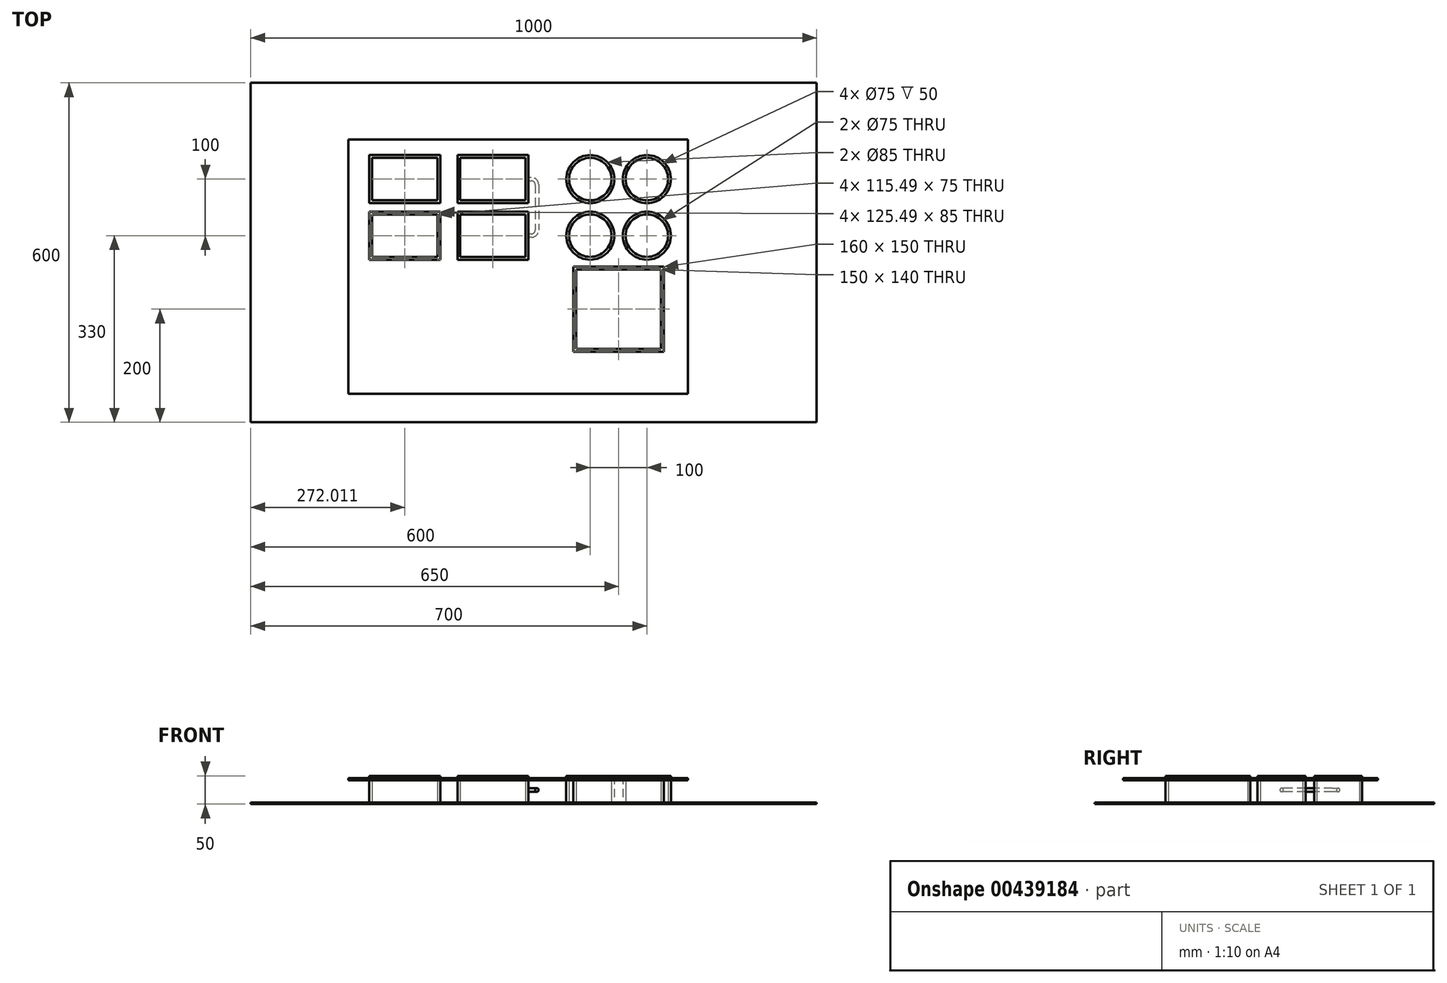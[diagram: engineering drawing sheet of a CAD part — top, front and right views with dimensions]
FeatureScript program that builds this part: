
annotation { "Feature Type Name" : "Feature", "Feature Type Description" : "" }
export const myFeature = defineFeature(function(context is Context, id is Id, definition is map)
    precondition{}
    {
        {
            var Q0;
            Q0=qCreatedBy(makeId("Top.planeOp"),FACE);
            var sketch = newSketch(context, id + "F0", { "sketchPlane" : qUnion([Q0])});
            skLineSegment(sketch, "E0.bottom", {"start": v(50, -50) * mm, "end": v(-50, -50) * mm, "construction": true});
            skLineSegment(sketch, "E0.top", {"start": v(50, 50) * mm, "end": v(-50, 50) * mm, "construction": true});
            skLineSegment(sketch, "E0.left", {"start": v(50, -50) * mm, "end": v(50, 50) * mm, "construction": true});
            skLineSegment(sketch, "E0.right", {"start": v(-50, -50) * mm, "end": v(-50, 50) * mm, "construction": true});
            skPoint(sketch, "E0.middle", {"position": v(0, 0) * mm});
            skCircle(sketch, "E1", {"center": v(-50, 50) * mm, "radius": 37.5 * mm});
            skCircle(sketch, "E2", {"center": v(-50, -50) * mm, "radius": 37.5 * mm});
            skCircle(sketch, "E3", {"center": v(50, -50) * mm, "radius": 37.5 * mm});
            skCircle(sketch, "E4", {"center": v(50, 50) * mm, "radius": 37.5 * mm});
            skLineSegment(sketch, "E5.bottom", {"start": v(75, -110) * mm, "end": v(-75, -110) * mm});
            skLineSegment(sketch, "E5.top", {"start": v(75, -250) * mm, "end": v(-75, -250) * mm});
            skLineSegment(sketch, "E5.left", {"start": v(75, -110) * mm, "end": v(75, -250) * mm});
            skLineSegment(sketch, "E5.right", {"start": v(-75, -110) * mm, "end": v(-75, -250) * mm});
            skPoint(sketch, "E5.middle", {"position": v(0, -180) * mm});
            skCircle(sketch, "E6.0", {"center": v(-50, -50) * mm, "radius": 42.5 * mm});
            skCircle(sketch, "E7.0", {"center": v(-50, 50) * mm, "radius": 42.5 * mm});
            skCircle(sketch, "E8.0", {"center": v(50, 50) * mm, "radius": 42.5 * mm});
            skCircle(sketch, "E9.0", {"center": v(50, -50) * mm, "radius": 42.5 * mm});
            skLineSegment(sketch, "E10.0", {"start": v(80, -105) * mm, "end": v(80, -255) * mm});
            skLineSegment(sketch, "E10.1", {"start": v(80, -105) * mm, "end": v(-80, -105) * mm});
            skLineSegment(sketch, "E10.2", {"start": v(-80, -105) * mm, "end": v(-80, -255) * mm});
            skLineSegment(sketch, "E10.3", {"start": v(80, -255) * mm, "end": v(-80, -255) * mm});
            skLineSegment(sketch, "E11.bottom", {"start": v(-222.01, -50) * mm, "end": v(-377.99, -50) * mm, "construction": true});
            skLineSegment(sketch, "E11.top", {"start": v(-222.01, 50) * mm, "end": v(-377.99, 50) * mm, "construction": true});
            skLineSegment(sketch, "E11.left", {"start": v(-222.01, -50) * mm, "end": v(-222.01, 50) * mm, "construction": true});
            skLineSegment(sketch, "E11.right", {"start": v(-377.99, -50) * mm, "end": v(-377.99, 50) * mm, "construction": true});
            skPoint(sketch, "E11.middle", {"position": v(-300, 0) * mm});
            skPoint(sketch, "E11.middle.positionSnap0", {"position": v(-50, 0) * mm});
            skPoint(sketch, "E11.centerSnap0", {"position": v(-50, 0) * mm});
            skLineSegment(sketch, "E12.bottom", {"start": v(-164.27, 12.5) * mm, "end": v(-279.75, 12.5) * mm});
            skLineSegment(sketch, "E12.top", {"start": v(-164.27, 87.5) * mm, "end": v(-279.75, 87.5) * mm});
            skLineSegment(sketch, "E12.left", {"start": v(-164.27, 12.5) * mm, "end": v(-164.27, 87.5) * mm});
            skLineSegment(sketch, "E12.right", {"start": v(-279.75, 12.5) * mm, "end": v(-279.75, 87.5) * mm});
            skPoint(sketch, "E12.middle", {"position": v(-222.01, 50) * mm});
            skLineSegment(sketch, "E13.bottom", {"start": v(-435.73, 87.5) * mm, "end": v(-320.25, 87.5) * mm});
            skLineSegment(sketch, "E13.top", {"start": v(-435.73, 12.5) * mm, "end": v(-320.25, 12.5) * mm});
            skLineSegment(sketch, "E13.left", {"start": v(-435.73, 87.5) * mm, "end": v(-435.73, 12.5) * mm});
            skLineSegment(sketch, "E13.right", {"start": v(-320.25, 87.5) * mm, "end": v(-320.25, 12.5) * mm});
            skPoint(sketch, "E13.middle", {"position": v(-377.99, 50) * mm});
            skLineSegment(sketch, "E14.bottom", {"start": v(-435.73, -87.5) * mm, "end": v(-320.25, -87.5) * mm});
            skLineSegment(sketch, "E14.top", {"start": v(-435.73, -12.5) * mm, "end": v(-320.25, -12.5) * mm});
            skLineSegment(sketch, "E14.left", {"start": v(-435.73, -87.5) * mm, "end": v(-435.73, -12.5) * mm});
            skLineSegment(sketch, "E14.right", {"start": v(-320.25, -87.5) * mm, "end": v(-320.25, -12.5) * mm});
            skPoint(sketch, "E14.middle", {"position": v(-377.99, -50) * mm});
            skLineSegment(sketch, "E15.bottom", {"start": v(-164.27, -87.5) * mm, "end": v(-279.75, -87.5) * mm});
            skLineSegment(sketch, "E15.top", {"start": v(-164.27, -12.5) * mm, "end": v(-279.75, -12.5) * mm});
            skLineSegment(sketch, "E15.left", {"start": v(-164.27, -87.5) * mm, "end": v(-164.27, -12.5) * mm});
            skLineSegment(sketch, "E15.right", {"start": v(-279.75, -87.5) * mm, "end": v(-279.75, -12.5) * mm});
            skPoint(sketch, "E15.middle", {"position": v(-222.01, -50) * mm});
            skLineSegment(sketch, "E16.0", {"start": v(-440.73, 92.5) * mm, "end": v(-440.73, 7.5) * mm});
            skLineSegment(sketch, "E16.1", {"start": v(-440.73, 92.5) * mm, "end": v(-315.25, 92.5) * mm});
            skLineSegment(sketch, "E16.2", {"start": v(-315.25, 92.5) * mm, "end": v(-315.25, 7.5) * mm});
            skLineSegment(sketch, "E16.3", {"start": v(-440.73, 7.5) * mm, "end": v(-315.25, 7.5) * mm});
            skLineSegment(sketch, "E17.0", {"start": v(-284.75, 7.5) * mm, "end": v(-284.75, 92.5) * mm});
            skLineSegment(sketch, "E17.1", {"start": v(-159.27, 7.5) * mm, "end": v(-284.75, 7.5) * mm});
            skLineSegment(sketch, "E17.2", {"start": v(-159.27, 7.5) * mm, "end": v(-159.27, 92.5) * mm});
            skLineSegment(sketch, "E17.3", {"start": v(-159.27, 92.5) * mm, "end": v(-284.75, 92.5) * mm});
            skLineSegment(sketch, "E18.0", {"start": v(-440.73, -92.5) * mm, "end": v(-315.25, -92.5) * mm});
            skLineSegment(sketch, "E18.1", {"start": v(-440.73, -92.5) * mm, "end": v(-440.73, -7.5) * mm});
            skLineSegment(sketch, "E18.2", {"start": v(-440.73, -7.5) * mm, "end": v(-315.25, -7.5) * mm});
            skLineSegment(sketch, "E18.3", {"start": v(-315.25, -92.5) * mm, "end": v(-315.25, -7.5) * mm});
            skLineSegment(sketch, "E19.0", {"start": v(-159.27, -92.5) * mm, "end": v(-284.75, -92.5) * mm});
            skLineSegment(sketch, "E19.1", {"start": v(-159.27, -92.5) * mm, "end": v(-159.27, -7.5) * mm});
            skLineSegment(sketch, "E19.2", {"start": v(-159.27, -7.5) * mm, "end": v(-284.75, -7.5) * mm});
            skLineSegment(sketch, "E19.3", {"start": v(-284.75, -92.5) * mm, "end": v(-284.75, -7.5) * mm});
            skSolve(sketch);
        }
        {
            var Q0;
            Q0 = qSketchRegion(id + "F0", true);
            extrude(context, id + "F1", {"entities" : qUnion([Q0]), "depth" : 50 * mm});
        }
        {
            var Q0;
            Q0=qCreatedBy(makeId("Top.planeOp"),FACE);
            var sketch = newSketch(context, id + "F2", { "sketchPlane" : qUnion([Q0])});
            skLineSegment(sketch, "E20.bottom", {"start": v(-650, 220) * mm, "end": v(350, 220) * mm});
            skLineSegment(sketch, "E20.top", {"start": v(-650, -380) * mm, "end": v(350, -380) * mm});
            skLineSegment(sketch, "E20.left", {"start": v(-650, 220) * mm, "end": v(-650, -380) * mm});
            skLineSegment(sketch, "E20.right", {"start": v(350, 220) * mm, "end": v(350, -380) * mm});
            skSolve(sketch);
        }
        {
            var Q0;
            Q0 = qSketchRegion(id + "F2", true);
            extrude(context, id + "F3", {"entities" : qUnion([Q0]), "depth" : 3 * mm});
        }
        {
            var Q0;
            Q0=qCreatedBy(makeId("Top.planeOp"),FACE);
            var sketch = newSketch(context, id + "F4", { "sketchPlane" : qUnion([Q0])});
            skLineSegment(sketch, "E21.0", {"start": v(-435.73, 87.5) * mm, "end": v(-435.73, 12.5) * mm});
            skLineSegment(sketch, "E22.0", {"start": v(-435.73, 87.5) * mm, "end": v(-320.25, 87.5) * mm});
            skLineSegment(sketch, "E23.0", {"start": v(-320.25, 87.5) * mm, "end": v(-320.25, 12.5) * mm});
            skLineSegment(sketch, "E24.0", {"start": v(-435.73, 12.5) * mm, "end": v(-320.25, 12.5) * mm});
            skLineSegment(sketch, "E25.0", {"start": v(-279.75, 12.5) * mm, "end": v(-279.75, 87.5) * mm});
            skLineSegment(sketch, "E26.0", {"start": v(-164.27, 87.5) * mm, "end": v(-279.75, 87.5) * mm});
            skLineSegment(sketch, "E27.0", {"start": v(-164.27, 12.5) * mm, "end": v(-164.27, 87.5) * mm});
            skLineSegment(sketch, "E28.0", {"start": v(-164.27, 12.5) * mm, "end": v(-279.75, 12.5) * mm});
            skLineSegment(sketch, "E29.0", {"start": v(-164.27, -12.5) * mm, "end": v(-279.75, -12.5) * mm});
            skLineSegment(sketch, "E30.0", {"start": v(-164.27, -87.5) * mm, "end": v(-164.27, -12.5) * mm});
            skLineSegment(sketch, "E31.0", {"start": v(-164.27, -87.5) * mm, "end": v(-279.75, -87.5) * mm});
            skLineSegment(sketch, "E32.0", {"start": v(-279.75, -87.5) * mm, "end": v(-279.75, -12.5) * mm});
            skLineSegment(sketch, "E33.0", {"start": v(-320.25, -87.5) * mm, "end": v(-320.25, -12.5) * mm});
            skLineSegment(sketch, "E34.0", {"start": v(-435.73, -12.5) * mm, "end": v(-320.25, -12.5) * mm});
            skLineSegment(sketch, "E35.0", {"start": v(-435.73, -87.5) * mm, "end": v(-435.73, -12.5) * mm});
            skLineSegment(sketch, "E36.0", {"start": v(-435.73, -87.5) * mm, "end": v(-320.25, -87.5) * mm});
            skCircle(sketch, "E37.0", {"center": v(-50, 50) * mm, "radius": 37.5 * mm});
            skCircle(sketch, "E38.0", {"center": v(-50, -50) * mm, "radius": 37.5 * mm});
            skCircle(sketch, "E39.0", {"center": v(50, 50) * mm, "radius": 37.5 * mm});
            skCircle(sketch, "E40.0", {"center": v(50, -50) * mm, "radius": 37.5 * mm});
            skLineSegment(sketch, "E41.0", {"start": v(75, -110) * mm, "end": v(-75, -110) * mm});
            skLineSegment(sketch, "E42.0", {"start": v(-75, -110) * mm, "end": v(-75, -250) * mm});
            skLineSegment(sketch, "E43.0", {"start": v(75, -250) * mm, "end": v(-75, -250) * mm});
            skLineSegment(sketch, "E44.0", {"start": v(75, -110) * mm, "end": v(75, -250) * mm});
            skSolve(sketch);
        }
        {
            var Q0;
            Q0 = qSketchRegion(id + "F4", true);
            extrude(context, id + "F5", {"entities" : qUnion([Q0]), "depth" : 42.7 * mm});
        }
        {
            var Q0;
            Q0=makeQuery(id+"F1.opExtrude","SWEPT_FACE",FACE,{"disambiguationData":[OSD([sQuery(id+"F0.wireOp",EDGE,"E17.2")])]});
            var sketch = newSketch(context, id + "F6", { "sketchPlane" : qUnion([Q0])});
            skLineSegment(sketch, "E45", {"start": v(50, 50) * mm, "end": v(50, 0) * mm, "construction": true});
            skLineSegment(sketch, "E46", {"start": v(7.5, 25) * mm, "end": v(92.5, 25) * mm, "construction": true});
            skCircle(sketch, "E47", {"center": v(50, 25) * mm, "radius": 3 * mm});
            skLineSegment(sketch, "E48.0", {"start": v(-92.5, 50) * mm, "end": v(-7.5, 50) * mm, "construction": true});
            skLineSegment(sketch, "E49.0", {"start": v(-92.5, 50) * mm, "end": v(-92.5, 0) * mm, "construction": true});
            skLineSegment(sketch, "E50.0", {"start": v(-92.5, 0) * mm, "end": v(-7.5, 0) * mm, "construction": true});
            skLineSegment(sketch, "E51.0", {"start": v(-7.5, 50) * mm, "end": v(-7.5, 0) * mm, "construction": true});
            skLineSegment(sketch, "E52", {"start": v(-50, 50) * mm, "end": v(-50, 0) * mm, "construction": true});
            skLineSegment(sketch, "E53", {"start": v(-92.5, 25) * mm, "end": v(-7.5, 25) * mm});
            skCircle(sketch, "E54", {"center": v(-50, 25) * mm, "radius": 3 * mm});
            skSolve(sketch);
        }
        {
            var Q0;
            Q0=qCreatedBy(makeId("Top.planeOp"),FACE);
            var Q1;
            Q1=sQuery(id+"F6.wireOp",EDGE,"E53");
            cPlane(context, id + "F7", {"entities" : qUnion([Q0, Q1]), "cplaneType" : CPlaneType.LINE_ANGLE, "offset" : 24.6 * mm, "angle" : 0 * degree, "oppositeDirection" : true, "width" : 150 * mm, "height" : 150 * mm});
        }
        {
            var Q0;
            Q0=qCreatedBy(id+"F7.planeOp",FACE);
            var sketch = newSketch(context, id + "F8", { "sketchPlane" : qUnion([Q0])});
            skPoint(sketch, "E55.0", {"position": v(-159.27, -50) * mm});
            skPoint(sketch, "E56.0", {"position": v(-159.27, 50) * mm});
            skLineSegment(sketch, "E57", {"start": v(-159.27, -50) * mm, "end": v(-154.27, -50) * mm});
            skLineSegment(sketch, "E58", {"start": v(-144.27, -40) * mm, "end": v(-144.27, 40) * mm});
            skLineSegment(sketch, "E59", {"start": v(-154.27, 50) * mm, "end": v(-159.27, 50) * mm});
            skPoint(sketch, "E60.visualSharp", {"position": v(-144.27, -50) * mm});
            skArc(sketch, "E60.filletArc", {"start": v(-154.27, -50) * mm, "mid": v(-147.2, -47.07) * mm, "end": v(-144.27, -40) * mm});
            skPoint(sketch, "E61.visualSharp", {"position": v(-144.27, 50) * mm});
            skArc(sketch, "E61.filletArc", {"start": v(-144.27, 40) * mm, "mid": v(-147.2, 47.07) * mm, "end": v(-154.27, 50) * mm});
            skSolve(sketch);
        }
        {
            var Q0;
            Q0=makeQuery(id+"F6.imprint","IMPRINT",FACE,{"disambiguationData":[TD([[makeQuery(id+"F6.imprint","IMPRINT",EDGE,{"derivedFrom":sQuery(id+"F6.wireOp",EDGE,"E47")}),1.0]])]});
            var Q1;
            Q1 = qConstructionFilter(qBodyType(qCreatedBy(id + "F8" ,EDGE), BodyType.WIRE), ConstructionObject.NO);
            sweep(context, id + "F9", {"profiles" : qUnion([Q0]), "path" : qUnion([Q1])});
        }
        {
            var Q0;
            Q0=makeQuery(id+"F1.opExtrude","CAP_FACE",FACE,{"disambiguationData":[OSD([sQuery(id+"F0.wireOp",EDGE,"E15.bottom"),sQuery(id+"F0.wireOp",EDGE,"E15.top"),sQuery(id+"F0.wireOp",EDGE,"E15.left"),sQuery(id+"F0.wireOp",EDGE,"E15.right"),sQuery(id+"F0.wireOp",EDGE,"E19.0"),sQuery(id+"F0.wireOp",EDGE,"E19.1"),sQuery(id+"F0.wireOp",EDGE,"E19.2"),sQuery(id+"F0.wireOp",EDGE,"E19.3")])],"isStart":false});
            cPlane(context, id + "F10", {"entities" : qUnion([Q0]), "cplaneType" : CPlaneType.OFFSET, "offset" : 8 * mm, "oppositeDirection" : true, "width" : 150 * mm, "height" : 150 * mm});
        }
        {
            var Q0;
            Q0=qCreatedBy(id+"F10.planeOp",FACE);
            var sketch = newSketch(context, id + "F11", { "sketchPlane" : qUnion([Q0])});
            skLineSegment(sketch, "E62.bottom", {"start": v(-477.78, 120.1) * mm, "end": v(122.22, 120.1) * mm});
            skLineSegment(sketch, "E62.top", {"start": v(-477.78, -329.9) * mm, "end": v(122.22, -329.9) * mm});
            skLineSegment(sketch, "E62.left", {"start": v(-477.78, 120.1) * mm, "end": v(-477.78, -329.9) * mm});
            skLineSegment(sketch, "E62.right", {"start": v(122.22, 120.1) * mm, "end": v(122.22, -329.9) * mm});
            skLineSegment(sketch, "E63.0.0", {"start": v(-435.73, 87.5) * mm, "end": v(-435.73, 12.5) * mm});
            skLineSegment(sketch, "E63.0.1", {"start": v(-435.73, 12.5) * mm, "end": v(-320.25, 12.5) * mm});
            skLineSegment(sketch, "E63.0.2", {"start": v(-320.25, 12.5) * mm, "end": v(-320.25, 87.5) * mm});
            skLineSegment(sketch, "E63.0.3", {"start": v(-320.25, 87.5) * mm, "end": v(-435.73, 87.5) * mm});
            skLineSegment(sketch, "E64.0.0", {"start": v(-279.75, 12.5) * mm, "end": v(-164.27, 12.5) * mm});
            skLineSegment(sketch, "E64.0.1", {"start": v(-164.27, 12.5) * mm, "end": v(-164.27, 87.5) * mm});
            skLineSegment(sketch, "E64.0.2", {"start": v(-164.27, 87.5) * mm, "end": v(-279.75, 87.5) * mm});
            skLineSegment(sketch, "E64.0.3", {"start": v(-279.75, 87.5) * mm, "end": v(-279.75, 12.5) * mm});
            skLineSegment(sketch, "E65.0.0", {"start": v(-279.75, -12.5) * mm, "end": v(-279.75, -87.5) * mm});
            skLineSegment(sketch, "E65.0.1", {"start": v(-279.75, -87.5) * mm, "end": v(-164.27, -87.5) * mm});
            skLineSegment(sketch, "E65.0.2", {"start": v(-164.27, -87.5) * mm, "end": v(-164.27, -12.5) * mm});
            skLineSegment(sketch, "E65.0.3", {"start": v(-164.27, -12.5) * mm, "end": v(-279.75, -12.5) * mm});
            skLineSegment(sketch, "E66.0.0", {"start": v(-435.73, -12.5) * mm, "end": v(-435.73, -87.5) * mm});
            skLineSegment(sketch, "E66.0.1", {"start": v(-435.73, -87.5) * mm, "end": v(-320.25, -87.5) * mm});
            skLineSegment(sketch, "E66.0.2", {"start": v(-320.25, -87.5) * mm, "end": v(-320.25, -12.5) * mm});
            skLineSegment(sketch, "E66.0.3", {"start": v(-320.25, -12.5) * mm, "end": v(-435.73, -12.5) * mm});
            skCircle(sketch, "E67.0.0", {"center": v(-50, 50) * mm, "radius": 37.5 * mm});
            skCircle(sketch, "E68.0.0", {"center": v(50, 50) * mm, "radius": 37.5 * mm});
            skCircle(sketch, "E69.0.0", {"center": v(50, -50) * mm, "radius": 37.5 * mm});
            skCircle(sketch, "E70.0.0", {"center": v(-50, -50) * mm, "radius": 37.5 * mm});
            skLineSegment(sketch, "E71.0.0", {"start": v(75, -250) * mm, "end": v(75, -110) * mm});
            skLineSegment(sketch, "E71.0.1", {"start": v(75, -110) * mm, "end": v(-75, -110) * mm});
            skLineSegment(sketch, "E71.0.2", {"start": v(-75, -110) * mm, "end": v(-75, -250) * mm});
            skLineSegment(sketch, "E71.0.3", {"start": v(-75, -250) * mm, "end": v(75, -250) * mm});
            skLineSegment(sketch, "E72.0.0", {"start": v(-440.73, 92.5) * mm, "end": v(-440.73, 7.5) * mm});
            skLineSegment(sketch, "E72.0.1", {"start": v(-440.73, 7.5) * mm, "end": v(-315.25, 7.5) * mm});
            skLineSegment(sketch, "E72.0.2", {"start": v(-315.25, 7.5) * mm, "end": v(-315.25, 92.5) * mm});
            skLineSegment(sketch, "E72.0.3", {"start": v(-315.25, 92.5) * mm, "end": v(-440.73, 92.5) * mm});
            skLineSegment(sketch, "E73.0.0", {"start": v(-159.27, 7.5) * mm, "end": v(-159.27, 92.5) * mm});
            skLineSegment(sketch, "E73.0.1", {"start": v(-159.27, 92.5) * mm, "end": v(-284.75, 92.5) * mm});
            skLineSegment(sketch, "E73.0.2", {"start": v(-284.75, 92.5) * mm, "end": v(-284.75, 7.5) * mm});
            skLineSegment(sketch, "E73.0.3", {"start": v(-284.75, 7.5) * mm, "end": v(-159.27, 7.5) * mm});
            skLineSegment(sketch, "E73.1.0", {"start": v(-284.75, -7.5) * mm, "end": v(-284.75, -92.5) * mm});
            skLineSegment(sketch, "E73.1.1", {"start": v(-284.75, -92.5) * mm, "end": v(-159.27, -92.5) * mm});
            skLineSegment(sketch, "E73.1.2", {"start": v(-159.27, -92.5) * mm, "end": v(-159.27, -7.5) * mm});
            skLineSegment(sketch, "E73.1.3", {"start": v(-159.27, -7.5) * mm, "end": v(-284.75, -7.5) * mm});
            skLineSegment(sketch, "E73.2.0", {"start": v(-440.73, -92.5) * mm, "end": v(-315.25, -92.5) * mm});
            skLineSegment(sketch, "E73.2.1", {"start": v(-315.25, -92.5) * mm, "end": v(-315.25, -7.5) * mm});
            skLineSegment(sketch, "E73.2.2", {"start": v(-315.25, -7.5) * mm, "end": v(-440.73, -7.5) * mm});
            skLineSegment(sketch, "E73.2.3", {"start": v(-440.73, -7.5) * mm, "end": v(-440.73, -92.5) * mm});
            skCircle(sketch, "E73.3.0", {"center": v(-50, 50) * mm, "radius": 42.5 * mm});
            skCircle(sketch, "E73.4.0", {"center": v(-50, -50) * mm, "radius": 42.5 * mm});
            skLineSegment(sketch, "E73.5.0", {"start": v(-80, -255) * mm, "end": v(80, -255) * mm});
            skLineSegment(sketch, "E73.5.1", {"start": v(80, -255) * mm, "end": v(80, -105) * mm});
            skLineSegment(sketch, "E73.5.2", {"start": v(80, -105) * mm, "end": v(-80, -105) * mm});
            skLineSegment(sketch, "E73.5.3", {"start": v(-80, -105) * mm, "end": v(-80, -255) * mm});
            skSolve(sketch);
        }
        {
            var Q0;
            Q0 = qSketchRegion(id + "F11", true);
            extrude(context, id + "F12", {"entities" : qUnion([Q0]), "depth" : 4 * mm});
        }
    });
